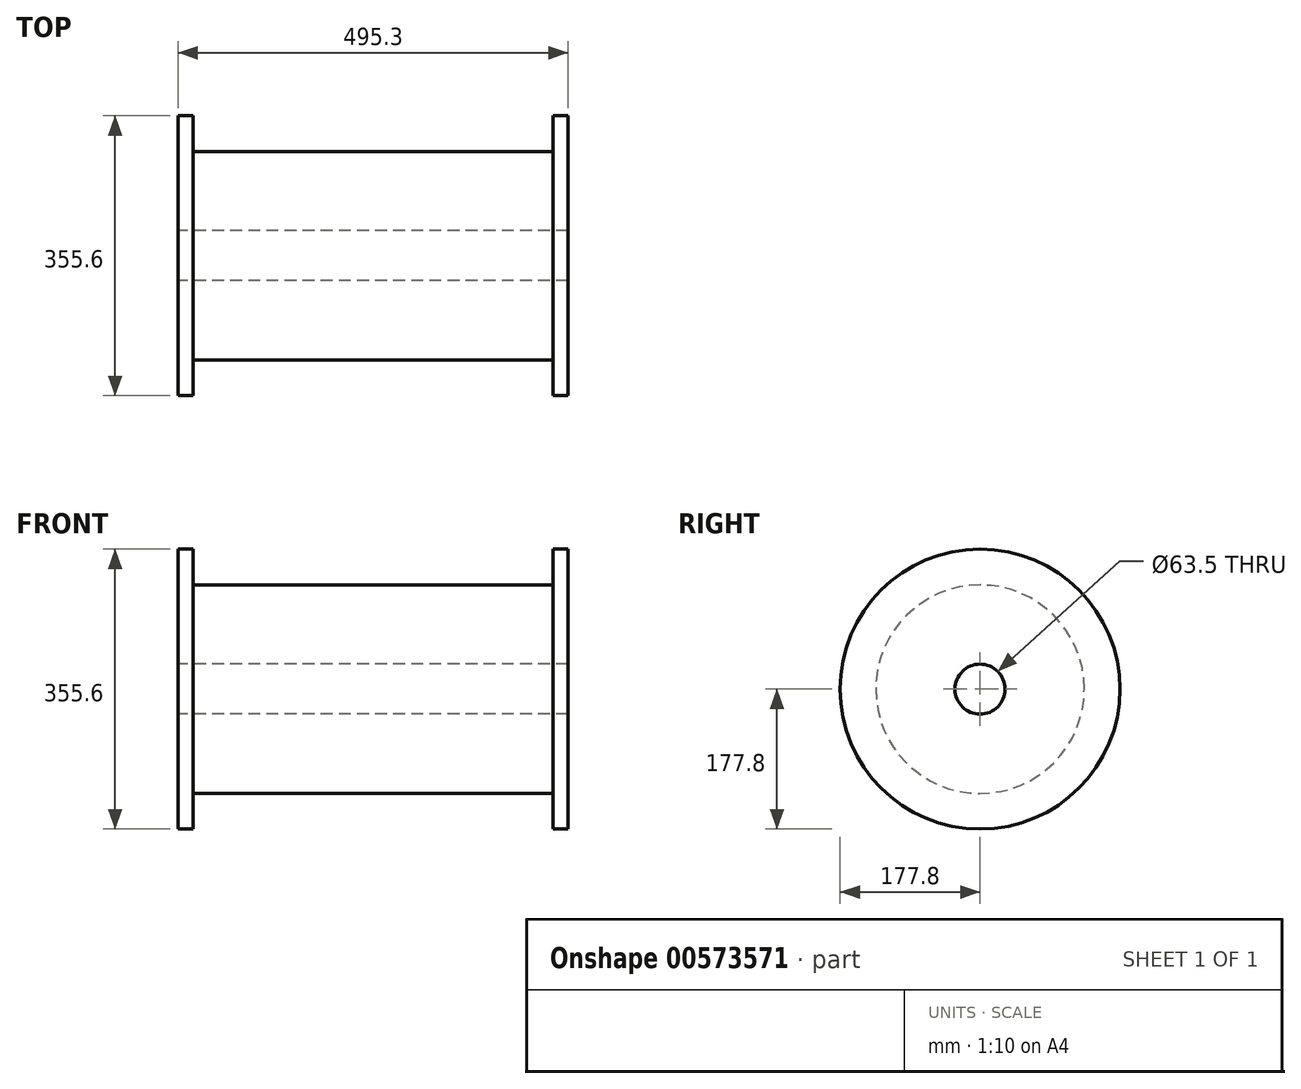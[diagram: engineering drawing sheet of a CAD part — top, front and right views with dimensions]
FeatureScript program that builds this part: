
annotation { "Feature Type Name" : "Feature", "Feature Type Description" : "" }
export const myFeature = defineFeature(function(context is Context, id is Id, definition is map)
    precondition{}
    {
        {
            var Q0;
            Q0=qCreatedBy(makeId("Front.planeOp"),FACE);
            var sketch = newSketch(context, id + "F0", { "sketchPlane" : qUnion([Q0])});
            skPoint(sketch, "E0", {"position": v(-247.65, 0) * mm});
            skPoint(sketch, "E1", {"position": v(247.65, 0) * mm});
            skLineSegment(sketch, "E2", {"start": v(-247.65, 0) * mm, "end": v(247.65, 0) * mm});
            skLineSegment(sketch, "E3", {"start": v(247.65, 177.8) * mm, "end": v(228.6, 177.8) * mm});
            skLineSegment(sketch, "E4", {"start": v(228.6, 177.8) * mm, "end": v(228.6, 132.43) * mm});
            skLineSegment(sketch, "E5", {"start": v(228.6, 132.43) * mm, "end": v(-228.6, 132.43) * mm});
            skLineSegment(sketch, "E6", {"start": v(-228.6, 132.43) * mm, "end": v(-228.6, 177.8) * mm});
            skLineSegment(sketch, "E7", {"start": v(-228.6, 177.8) * mm, "end": v(-247.65, 177.8) * mm});
            skLineSegment(sketch, "E8", {"start": v(-247.65, 177.8) * mm, "end": v(-247.65, 0) * mm});
            skLineSegment(sketch, "E9", {"start": v(247.65, 177.8) * mm, "end": v(247.65, 0) * mm});
            skSolve(sketch);
        }
        {
            var Q0;
            Q0 = qSketchRegion(id + "F0", true);
            var Q1;
            Q1=sQuery(id+"F0.wireOp",EDGE,"E2");
            revolve(context, id + "F1", {"entities" : qUnion([Q0]), "axis" : qUnion([Q1]), "revolveType" : RevolveType.FULL});
        }
        {
            var Q0;
            Q0=makeQuery(id+"F1.opRevolve","SWEPT_FACE",FACE,{"disambiguationData":[OSD([sQuery(id+"F0.wireOp",EDGE,"E8")])]});
            var sketch = newSketch(context, id + "F2", { "sketchPlane" : qUnion([Q0])});
            skCircle(sketch, "E10", {"center": v(0, 0) * mm, "radius": 31.75 * mm});
            skSolve(sketch);
        }
        {
            var Q0;
            Q0 = qSketchRegion(id + "F2", true);
            extrude(context, id + "F3", {"entities" : qUnion([Q0]), "operationType" : NewBodyOperationType.REMOVE, "endBound" : BoundingType.THROUGH_ALL, "oppositeDirection" : true, "depth" : 25.4 * mm, "offsetDistance" : 25.4 * mm});
        }
    });
